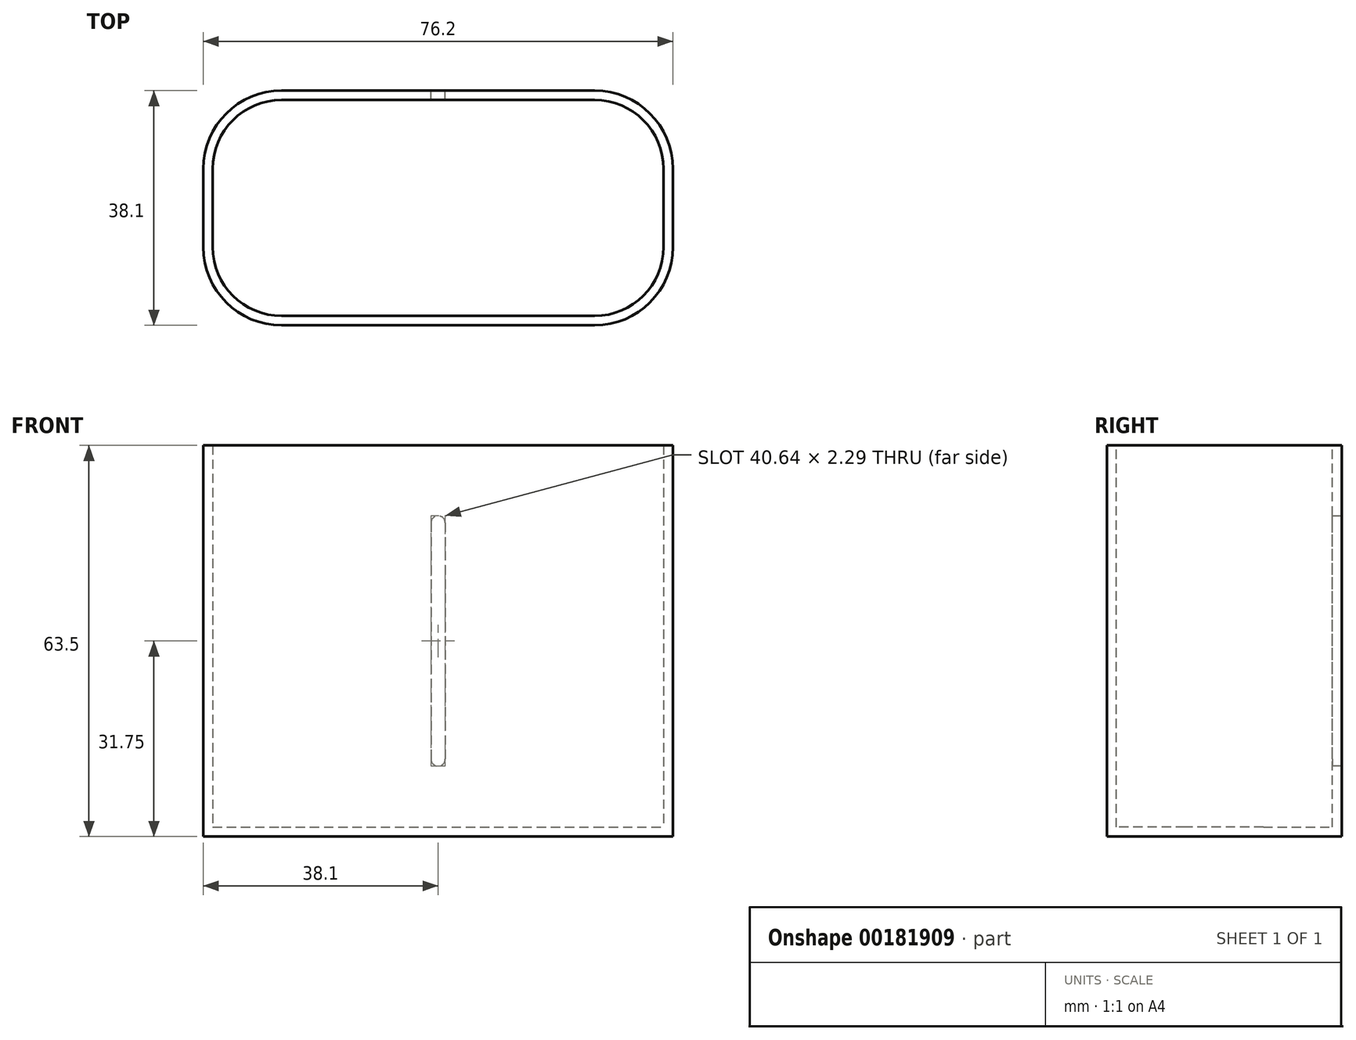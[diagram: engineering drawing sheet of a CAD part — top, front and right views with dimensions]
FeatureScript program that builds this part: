
annotation { "Feature Type Name" : "Feature", "Feature Type Description" : "" }
export const myFeature = defineFeature(function(context is Context, id is Id, definition is map)
    precondition{}
    {
        {
            var Q0;
            Q0=qCreatedBy(makeId("Top.planeOp"),FACE);
            var sketch = newSketch(context, id + "F0", { "sketchPlane" : qUnion([Q0])});
            skLineSegment(sketch, "E0.bottom", {"start": v(-38.1, 19.05) * mm, "end": v(38.1, 19.05) * mm});
            skLineSegment(sketch, "E0.top", {"start": v(-38.1, -19.05) * mm, "end": v(38.1, -19.05) * mm});
            skLineSegment(sketch, "E0.left", {"start": v(-38.1, 19.05) * mm, "end": v(-38.1, -19.05) * mm});
            skLineSegment(sketch, "E0.right", {"start": v(38.1, 19.05) * mm, "end": v(38.1, -19.05) * mm});
            skPoint(sketch, "E1", {"position": v(0, 19.05) * mm});
            skPoint(sketch, "E2", {"position": v(-38.1, 0) * mm});
            skSolve(sketch);
        }
        {
            var Q0;
            Q0 = qSketchRegion(id + "F0", true);
            extrude(context, id + "F1", {"entities" : qUnion([Q0]), "depth" : 63.5 * mm});
        }
        {
            var Q0;
            Q0=makeQuery(id+"F1.opExtrude","SWEPT_EDGE",EDGE,{"disambiguationData":[OSD([sQuery(id+"F0.wireOp",EDGE,"E0.top"),sQuery(id+"F0.wireOp",EDGE,"E0.right")])]});
            var Q1;
            Q1=makeQuery(id+"F1.opExtrude","SWEPT_EDGE",EDGE,{"disambiguationData":[OSD([sQuery(id+"F0.wireOp",EDGE,"E0.bottom"),sQuery(id+"F0.wireOp",EDGE,"E0.right")])]});
            var Q2;
            Q2=makeQuery(id+"F1.opExtrude","SWEPT_EDGE",EDGE,{"disambiguationData":[OSD([sQuery(id+"F0.wireOp",EDGE,"E0.top"),sQuery(id+"F0.wireOp",EDGE,"E0.left")])]});
            var Q3;
            Q3=makeQuery(id+"F1.opExtrude","SWEPT_EDGE",EDGE,{"disambiguationData":[OSD([sQuery(id+"F0.wireOp",EDGE,"E0.bottom"),sQuery(id+"F0.wireOp",EDGE,"E0.left")])]});
            fillet(context, id + "F2", {"entities" : qUnion([Q0, Q1, Q2, Q3]), "radius" : 12.7 * mm, "tangentPropagation" : true, "allowEdgeOverflow" : false});
        }
        {
            var Q0;
            Q0=makeQuery(id+"F1.opExtrude","CAP_FACE",FACE,{"disambiguationData":[OSD([sQuery(id+"F0.wireOp",EDGE,"E0.bottom"),sQuery(id+"F0.wireOp",EDGE,"E0.top"),sQuery(id+"F0.wireOp",EDGE,"E0.left"),sQuery(id+"F0.wireOp",EDGE,"E0.right")])],"isStart":false});
            shell(context, id + "F3", {"entities" : qUnion([Q0]), "thickness" : 1.52 * mm});
        }
        {
            var Q0;
            Q0=makeQuery(id+"F1.opExtrude","SWEPT_FACE",FACE,{"disambiguationData":[OSD([sQuery(id+"F0.wireOp",EDGE,"E0.bottom")])]});
            var sketch = newSketch(context, id + "F4", { "sketchPlane" : qUnion([Q0])});
            skLineSegment(sketch, "E3.bottom", {"start": v(-1.14, 52.07) * mm, "end": v(1.14, 52.07) * mm});
            skLineSegment(sketch, "E3.top", {"start": v(-1.14, 11.43) * mm, "end": v(1.14, 11.43) * mm});
            skLineSegment(sketch, "E3.left", {"start": v(-1.14, 52.07) * mm, "end": v(-1.14, 11.43) * mm});
            skLineSegment(sketch, "E3.right", {"start": v(1.14, 52.07) * mm, "end": v(1.14, 11.43) * mm});
            skPoint(sketch, "E4", {"position": v(0, 52.07) * mm});
            skPoint(sketch, "E5", {"position": v(1.14, 31.75) * mm});
            skPoint(sketch, "E6", {"position": v(25.4, 31.75) * mm});
            skSolve(sketch);
        }
        {
            var Q0;
            Q0 = qSketchRegion(id + "F4", true);
            var Q1;
            Q1=makeQuery(id+"F3.opShell","OFFSET_FACE",FACE,{"disambiguationData":[OSD([sQuery(id+"F0.wireOp",EDGE,"E0.bottom")])]});
            extrude(context, id + "F5", {"entities" : qUnion([Q0]), "operationType" : NewBodyOperationType.REMOVE, "endBound" : BoundingType.UP_TO_SURFACE, "oppositeDirection" : true, "endBoundEntityFace" : qUnion([Q1]), "depth" : 25.4 * mm});
        }
        {
            var Q0;
            Q0=makeQuery(id+"F5.boolean.opBoolean","COPY",EDGE,{"derivedFrom":makeQuery(id+"F5.opExtrude","SWEPT_EDGE",EDGE,{"disambiguationData":[OSD([sQuery(id+"F4.wireOp",EDGE,"E3.bottom"),sQuery(id+"F4.wireOp",EDGE,"E3.left")])]})});
            var Q1;
            Q1=makeQuery(id+"F5.boolean.opBoolean","COPY",EDGE,{"derivedFrom":makeQuery(id+"F5.opExtrude","SWEPT_EDGE",EDGE,{"disambiguationData":[OSD([sQuery(id+"F4.wireOp",EDGE,"E3.bottom"),sQuery(id+"F4.wireOp",EDGE,"E3.right")])]})});
            var Q2;
            Q2=makeQuery(id+"F5.boolean.opBoolean","COPY",EDGE,{"derivedFrom":makeQuery(id+"F5.opExtrude","SWEPT_EDGE",EDGE,{"disambiguationData":[OSD([sQuery(id+"F4.wireOp",EDGE,"E3.top"),sQuery(id+"F4.wireOp",EDGE,"E3.left")])]})});
            var Q3;
            Q3=makeQuery(id+"F5.boolean.opBoolean","COPY",EDGE,{"derivedFrom":makeQuery(id+"F5.opExtrude","SWEPT_EDGE",EDGE,{"disambiguationData":[OSD([sQuery(id+"F4.wireOp",EDGE,"E3.top"),sQuery(id+"F4.wireOp",EDGE,"E3.right")])]})});
            fillet(context, id + "F6", {"entities" : qUnion([Q0, Q1, Q2, Q3]), "radius" : 1.14 * mm, "tangentPropagation" : true, "allowEdgeOverflow" : false});
        }
    });
